# Revit family: Building-IEC309Connections-GEWISS-IEC309HP-90°_SURF_MOUNT_INLET_MANTLE_TERMINAL_125A_IP67
name_source: partatom
category: Apparecchi elettrici
units: mm (PartAtom-declared; Revit-internal decimal feet)

## family parameters
Condiviso = Sì
Host = Superficie
Mantenere orientamento annotazione = Sì
Punto di calcolo locali = Sì
Quota connettore circolare = Usa diametro
Taglio con vuoti quando caricato = No
Tipo di parte = Normale

## types (8) — shared parameters
BLOCCO = B=C
Breaking capacity at 1.1 Un = 156A
Catalogue = BUILDING
Corpo centrale = Default(2)
Electrocod = 2230
FORMULA = 1000 mm  [stored 3.28084 ft]
Frequency = 50/60 Hz
Glow wire test: = 850 °C (active parts) - 650 °C (passive parts)
IDF = 41552599-a9bc-4a44-b0c6-a7e5c48e472e
IDT = 65faf2d8742c4b6998c525a67799a263
IP degree = IP67
Immagine tipo = <Nessuno>
Insulation resistance = - 10 M?
L = 155 mm
Operating temperature: = -25 +55 °C
Piastra = Default(2)
Produttore = GEWISS S.p.A.
Prospetto di default = 1219 mm
Rated current (A) = 125
SEO = Inlet
SPinotto = Default(2)
Shock resistance = IK08
Spostamento_S = 930 mm
Technical sheet = https://www.gewiss.com
Terminal tightening capacity = 16-50mm² flexible cables - 25-70mm² rigid cables
Thermo-pressure with ball = 125 °C (active parts) - 80 °C (passive parts)
Total number of operations = -500
Type of wiring = Mantle terminal
Typology = 90° angled surface mounting inlet
URL = https://www.gewiss.com
Version file RFA = 21.11
W = 115 mm  [stored 0.377297 ft]

## per-type parameters (varying)
| type | Colour: | Descrizione | Modello | No. of poles | Rated voltage | Reference h |
| GW60462 - IP67 90°APPL.INLET 3P+E 125A 500V 7H | Black | IP67 90°APPL.INLET 3P+E 125A 500V 7H | GW60462 | 3P+E | 480-500V | 7 |
| GW60457 - IP67 90°APPL.INLET 3P+N+E 125A 110V 4H | Yellow | IP67 90°APPL.INLET 3P+N+E 125A 110V 4H | GW60457 | 3P+N+E | 100-130V | 4 |
| GW60463 - IP67 90°APPL.INLET 3P+N+E 125A 500V 7H | Black | IP67 90°APPL.INLET 3P+N+E 125A 500V 7H | GW60463 | 3P+N+E | 480-500V | 7 |
| GW60456 - IP67 90°APPL.INLET 3P+E 125A 110V 4H | Yellow | IP67 90°APPL.INLET 3P+E 125A 110V 4H | GW60456 | 3P+E | 100-130V | 4 |
| GW60458 - IP67 90°APPL.INLET 3P+E 125A 230V 9H | Blue | IP67 90°APPL.INLET 3P+E 125A 230V 9H | GW60458 | 3P+E | 200-250V | 9 |
| GW60461 - IP67 90°APPL.INLET 3P+N+E 125A 400V 6H | Red | IP67 90°APPL.INLET 3P+N+E 125A 400V 6H | GW60461 | 3P+N+E | 380-415V | 6 |
| GW60460 - IP67 90°APPL.INLET 3P+E 125A 400V 6H | Red | IP67 90°APPL.INLET 3P+E 125A 400V 6H | GW60460 | 3P+E | 380-415V | 6 |
| GW60459 - IP67 90°APPL.INLET 3P+N+E 125A 230V 9H | Blue | IP67 90°APPL.INLET 3P+N+E 125A 230V 9H | GW60459 | 3P+N+E | 200-250V | 9 |

note: [stored X ft] marks values corroborated as IEEE doubles in the binary element streams (Revit-internal decimal feet)

## geometry (parser evidence)
native form markers: Sweep x2
no freeform markers — native parametric forms only
